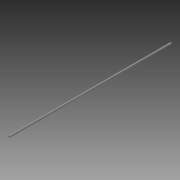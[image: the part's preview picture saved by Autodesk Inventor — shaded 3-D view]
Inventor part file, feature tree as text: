
AUTODESK INVENTOR PART (.ipt)
format: ipt  version: 2013 (Build 170138000, 138)  size: 66,048 bytes
history: native  units: in
note: dims shown in document units (in); Inventor stores cm internally (conversion verified against a paired STEP export)
features: extrude x1, sketch x1
ambient origin geometry x8: Origin, YZ Plane, XZ Plane, XY Plane, X Axis, Y Axis, Z Axis, Center Point
bodies: Solid1 (feature_tree)
feature tree (2):
  extrude  "Extrusion1"  Depth=0.091in
  sketch  "Sketch1"  dims[d0=0.675in d2=0.091in d3=62.75in d4=0.0in]
